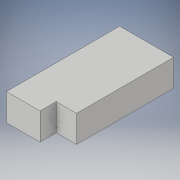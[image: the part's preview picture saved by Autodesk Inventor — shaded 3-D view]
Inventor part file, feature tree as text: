
AUTODESK INVENTOR PART (.ipt)
format: ipt  version: 2019.4 (Build 234330000, 330)  size: 98,816 bytes
history: native  units: mm
features: extrude x2, sketch x2
ambient origin geometry x8: Origin, YZ Plane, XZ Plane, XY Plane, X Axis, Y Axis, Z Axis, Center Point
bodies: Solid1 (feature_tree)
feature tree (4):
  extrude  "Extrusion1"  Depth=228.6mm
  extrude  "Extrusion2"  Depth=79.2mm
  sketch  "Sketch1"  dims[d0=127.0mm d1=228.6mm]
  sketch  "Sketch2"  dims[d2=63.5mm d3=0.0mm d4=79.2mm d5=38.1mm d6=0.0mm]
